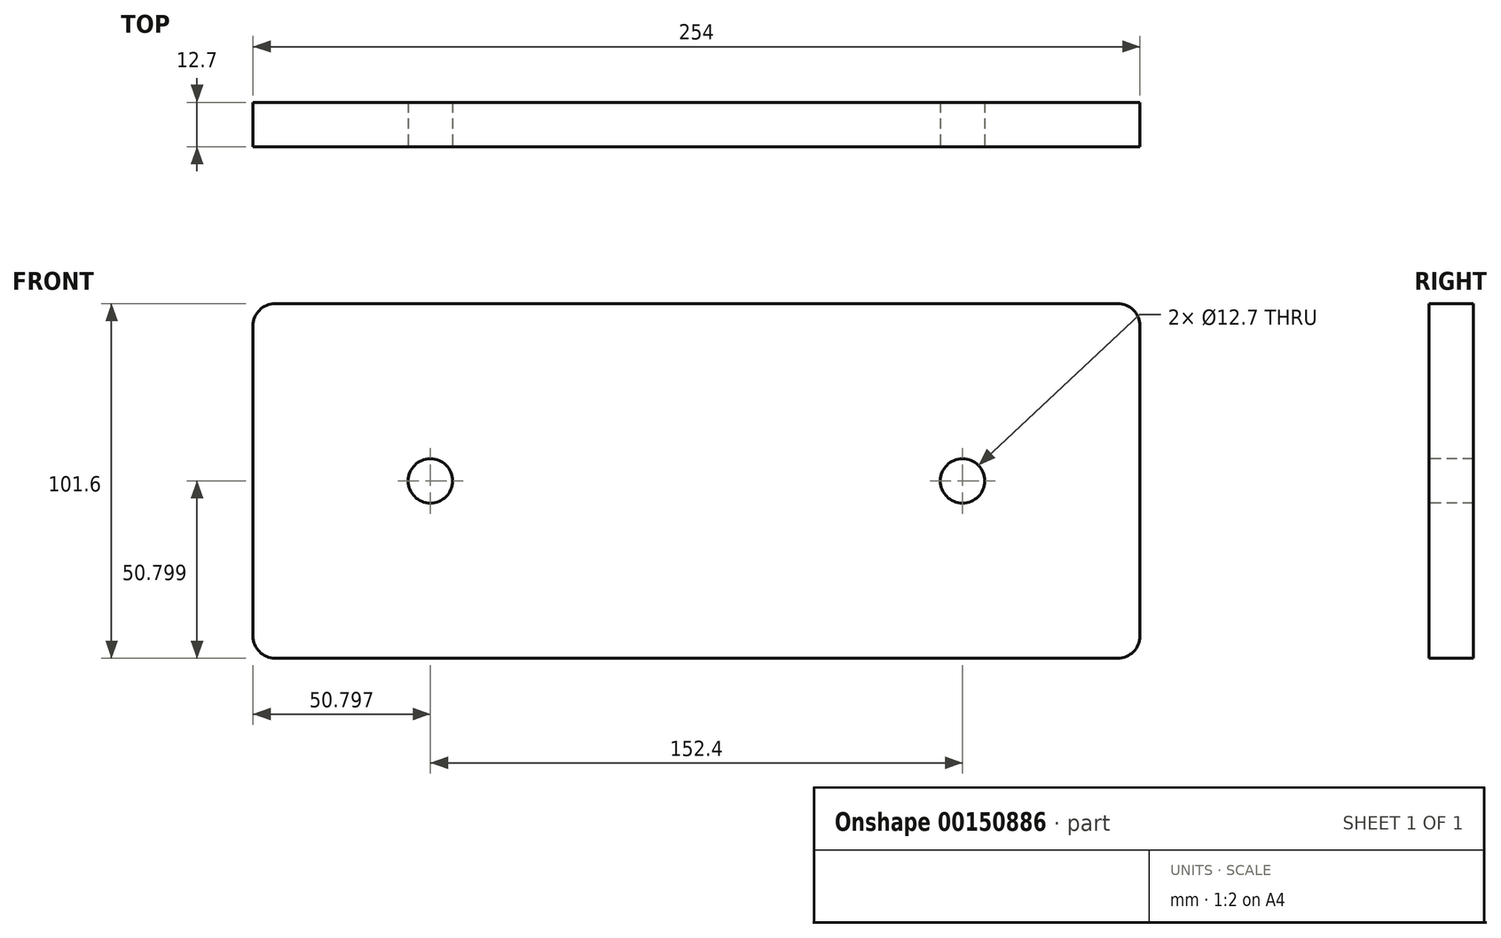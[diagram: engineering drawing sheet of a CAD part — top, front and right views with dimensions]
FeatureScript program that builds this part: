
annotation { "Feature Type Name" : "Feature", "Feature Type Description" : "" }
export const myFeature = defineFeature(function(context is Context, id is Id, definition is map)
    precondition{}
    {
        {
            var Q0;
            Q0=qCreatedBy(makeId("Front.planeOp"),FACE);
            var sketch = newSketch(context, id + "F0", { "sketchPlane" : qUnion([Q0])});
            skLineSegment(sketch, "E0.bottom", {"start": v(-42.08, 81.52) * mm, "end": v(199.22, 81.52) * mm});
            skLineSegment(sketch, "E0.top", {"start": v(-42.08, -20.08) * mm, "end": v(199.22, -20.08) * mm});
            skLineSegment(sketch, "E0.left", {"start": v(-48.43, 75.17) * mm, "end": v(-48.43, -13.73) * mm});
            skLineSegment(sketch, "E0.right", {"start": v(205.57, 75.17) * mm, "end": v(205.57, -13.73) * mm});
            skPoint(sketch, "E1.visualSharp", {"position": v(-48.43, 81.52) * mm});
            skArc(sketch, "E1.filletArc", {"start": v(-42.08, 81.52) * mm, "mid": v(-46.57, 79.66) * mm, "end": v(-48.43, 75.17) * mm});
            skPoint(sketch, "E2.visualSharp", {"position": v(205.57, 81.52) * mm});
            skArc(sketch, "E2.filletArc", {"start": v(205.57, 75.17) * mm, "mid": v(203.7, 79.66) * mm, "end": v(199.22, 81.52) * mm});
            skPoint(sketch, "E3.visualSharp", {"position": v(205.57, -20.08) * mm});
            skArc(sketch, "E3.filletArc", {"start": v(199.22, -20.08) * mm, "mid": v(203.7, -18.22) * mm, "end": v(205.57, -13.73) * mm});
            skPoint(sketch, "E4.visualSharp", {"position": v(-48.43, -20.08) * mm});
            skArc(sketch, "E4.filletArc", {"start": v(-48.43, -13.73) * mm, "mid": v(-46.57, -18.22) * mm, "end": v(-42.08, -20.08) * mm});
            skSolve(sketch);
        }
        {
            var Q0;
            Q0 = qSketchRegion(id + "F0", true);
            extrude(context, id + "F1", {"entities" : qUnion([Q0]), "depth" : 12.7 * mm});
        }
        {
            var Q0;
            Q0=makeQuery(id+"F1.opExtrude","CAP_FACE",FACE,{"disambiguationData":[OSD([sQuery(id+"F0.wireOp",EDGE,"E0.bottom"),sQuery(id+"F0.wireOp",EDGE,"E0.top"),sQuery(id+"F0.wireOp",EDGE,"E0.left"),sQuery(id+"F0.wireOp",EDGE,"E0.right"),sQuery(id+"F0.wireOp",EDGE,"E1.filletArc"),sQuery(id+"F0.wireOp",EDGE,"E2.filletArc"),sQuery(id+"F0.wireOp",EDGE,"E3.filletArc"),sQuery(id+"F0.wireOp",EDGE,"E4.filletArc")])],"isStart":false});
            var sketch = newSketch(context, id + "F2", { "sketchPlane" : qUnion([Q0])});
            skCircle(sketch, "E5", {"center": v(2.37, 30.72) * mm, "radius": 6.35 * mm});
            skCircle(sketch, "E6", {"center": v(154.77, 30.72) * mm, "radius": 6.35 * mm});
            skSolve(sketch);
        }
        {
            var Q0;
            Q0 = qSketchRegion(id + "F2", true);
            extrude(context, id + "F3", {"entities" : qUnion([Q0]), "operationType" : NewBodyOperationType.REMOVE, "oppositeDirection" : true, "depth" : 25.4 * mm});
        }
    });
